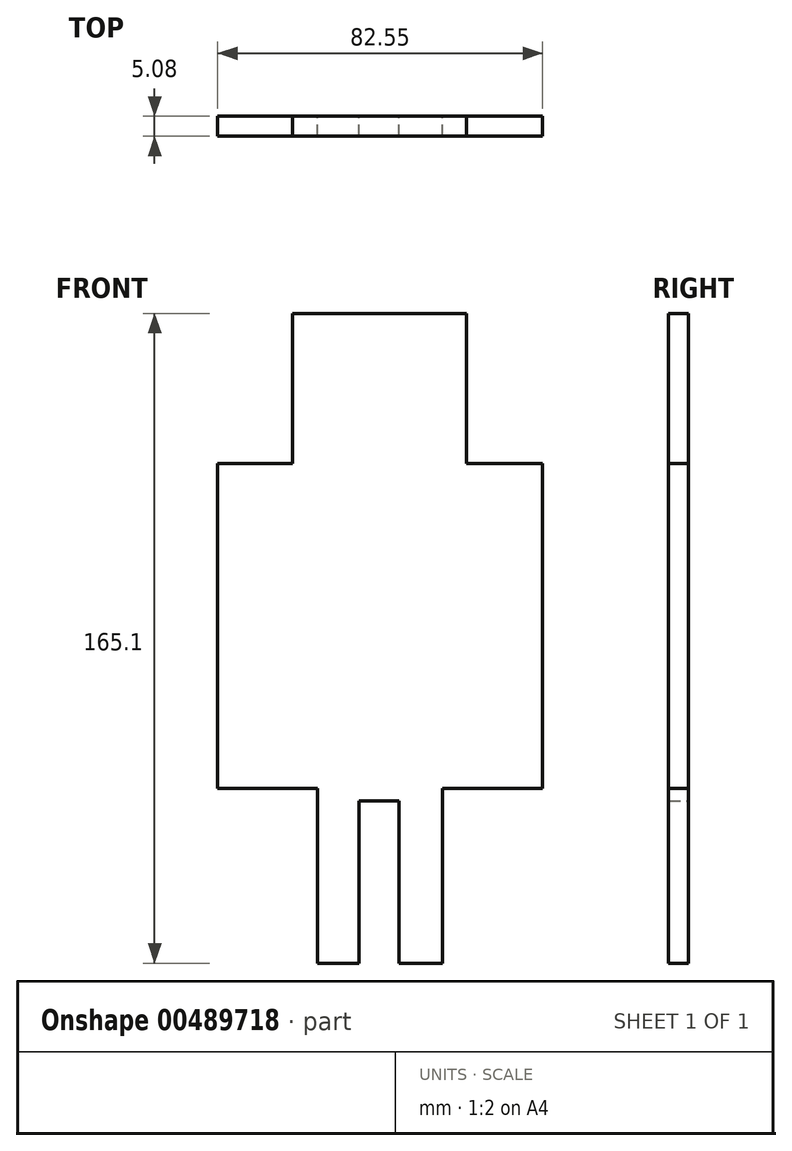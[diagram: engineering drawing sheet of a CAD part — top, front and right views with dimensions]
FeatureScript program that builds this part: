
annotation { "Feature Type Name" : "Feature", "Feature Type Description" : "" }
export const myFeature = defineFeature(function(context is Context, id is Id, definition is map)
    precondition{}
    {
        {
            var Q0;
            Q0=qCreatedBy(makeId("Front.planeOp"),FACE);
            var sketch = newSketch(context, id + "F0", { "sketchPlane" : qUnion([Q0])});
            skLineSegment(sketch, "E0.bottom", {"start": v(-89.98, 51.88) * mm, "end": v(-70.93, 51.88) * mm});
            skLineSegment(sketch, "E0.top", {"start": v(-64.58, -75.12) * mm, "end": v(-54.03, -75.12) * mm});
            skLineSegment(sketch, "E0.left", {"start": v(-89.98, 51.88) * mm, "end": v(-89.98, -30.67) * mm});
            skLineSegment(sketch, "E0.right", {"start": v(-7.43, 51.88) * mm, "end": v(-7.43, -30.67) * mm});
            skLineSegment(sketch, "E1.top", {"start": v(-89.98, -30.67) * mm, "end": v(-64.58, -30.67) * mm});
            skLineSegment(sketch, "E1.right", {"start": v(-64.58, -75.12) * mm, "end": v(-64.58, -30.67) * mm});
            skLineSegment(sketch, "E2", {"start": v(-32.83, -30.67) * mm, "end": v(-7.43, -30.67) * mm});
            skLineSegment(sketch, "E3.left", {"start": v(-32.83, -30.67) * mm, "end": v(-32.83, -75.12) * mm});
            skLineSegment(sketch, "E4.top", {"start": v(-54.03, -33.85) * mm, "end": v(-43.87, -33.85) * mm});
            skLineSegment(sketch, "E4.left", {"start": v(-54.03, -75.12) * mm, "end": v(-54.03, -33.85) * mm});
            skLineSegment(sketch, "E4.right", {"start": v(-43.87, -75.12) * mm, "end": v(-43.87, -33.85) * mm});
            skLineSegment(sketch, "E5.trimOffspring", {"start": v(-43.87, -75.12) * mm, "end": v(-32.83, -75.12) * mm});
            skLineSegment(sketch, "E6.bottom", {"start": v(-26.71, 51.88) * mm, "end": v(-26.48, 51.88) * mm});
            skLineSegment(sketch, "E7", {"start": v(-70.93, 51.88) * mm, "end": v(-89.98, 51.88) * mm});
            skLineSegment(sketch, "E8", {"start": v(-7.43, 51.88) * mm, "end": v(-26.48, 51.88) * mm});
            skLineSegment(sketch, "E9.top", {"start": v(-70.93, 89.98) * mm, "end": v(-26.71, 89.98) * mm});
            skLineSegment(sketch, "E9.left", {"start": v(-70.93, 51.88) * mm, "end": v(-70.93, 89.98) * mm});
            skLineSegment(sketch, "E9.right", {"start": v(-26.71, 51.88) * mm, "end": v(-26.71, 89.98) * mm});
            skLineSegment(sketch, "E10.trimOffspring", {"start": v(-26.71, 51.88) * mm, "end": v(-7.43, 51.88) * mm});
            skSolve(sketch);
        }
        {
            var Q0;
            Q0 = qSketchRegion(id + "F0", true);
            var Q1;
            Q1=makeQuery(id+"F0.imprint","IMPRINT",FACE,{"disambiguationData":[TD([[makeQuery(id+"F0.imprint","IMPRINT",EDGE,{"derivedFrom":sQuery(id+"F0.wireOp",EDGE,"E0.top")}),1.0]])]});
            extrude(context, id + "F1", {"entities" : qUnion([Q0, Q1]), "depth" : 5.08 * mm});
        }
    });
